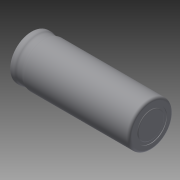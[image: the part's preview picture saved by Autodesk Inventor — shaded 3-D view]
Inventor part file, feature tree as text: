
AUTODESK INVENTOR PART (.ipt)
format: ipt  version: 2014 (Build 180170000, 170)  size: 162,304 bytes
history: native  units: mm
features: fillet x4, sketch x4, extrude x3, revolve x1, plane x1, mirror x1
ambient origin geometry x8: Origin, YZ Plane, XZ Plane, XY Plane, X Axis, Y Axis, Z Axis, Center Point
bodies: Volumenkörper1 (feature_tree)
feature tree (14):
  revolve  "Umdrehung1"
  plane  "Arbeitsebene1"
  fillet  "Rundung1"  Radius=49.8mm
  fillet  "Rundung2"  Radius=9.1mm
  extrude  "Extrusion1"  Depth=3.0mm
  mirror  "Spiegeln1"
  extrude  "Extrusion2"  TaperAngle=90.0deg  [1 undecoded]
  fillet  "Rundung3"  Radius=2.0mm
  extrude  "Extrusion3"  Depth=0.2mm
  fillet  "Rundung4"  Radius=0.2mm
  sketch  "Skizze1"  dims[d2=3.0mm d3=3.0mm]
  sketch  "Skizze2"  dims[d4=0.35mm d5=90.0deg d6=2.0mm]
  sketch  "Skizze3"  dims[d7=1.0mm d8=13.0mm d9=0.2mm d10=0.0mm]
  sketch  "Skizze4"  dims[d11=5.7mm d12=1.0mm d13=0.0mm d14=0.5mm d15=1.0mm d16=0.2mm d17=0.0mm d18=0.5mm]
note: 1 required parameter value undecoded (feature->parameter linkage not recoverable at this tier; creation-order binding heuristic only, values carry confidence <= 0.55)
